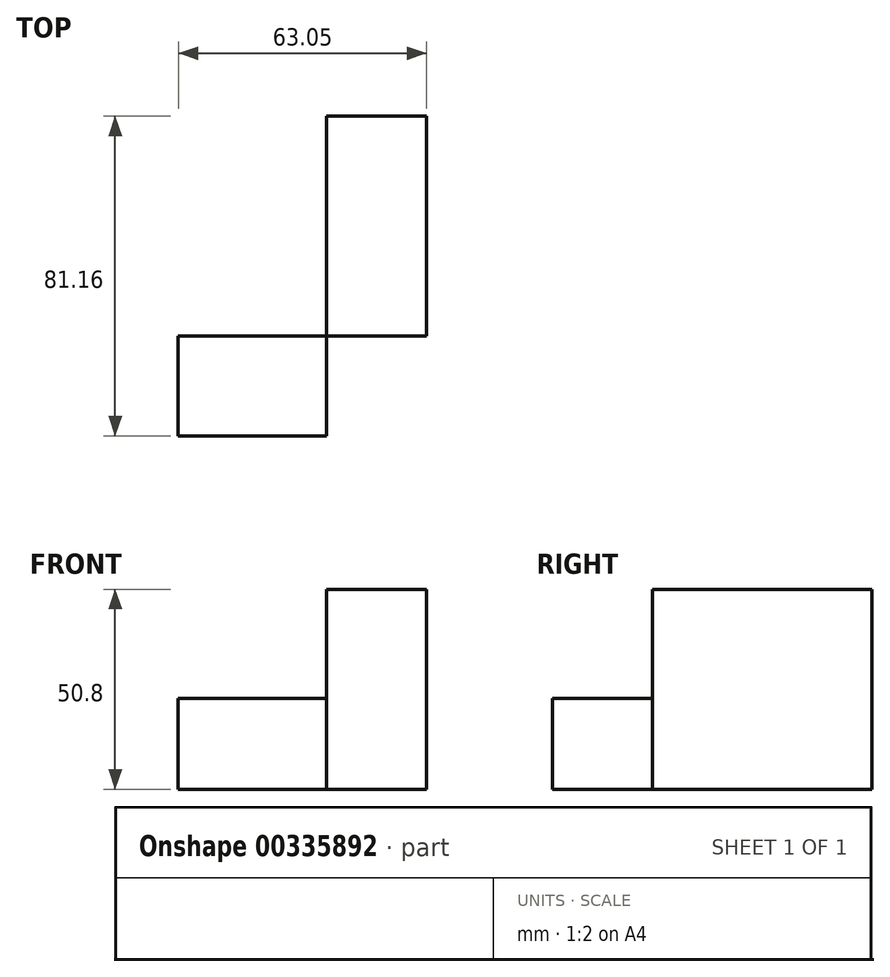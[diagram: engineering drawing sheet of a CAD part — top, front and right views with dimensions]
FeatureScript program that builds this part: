
annotation { "Feature Type Name" : "Feature", "Feature Type Description" : "" }
export const myFeature = defineFeature(function(context is Context, id is Id, definition is map)
    precondition{}
    {
        {
            var Q0;
            Q0=qCreatedBy(makeId("Right.planeOp"),FACE);
            var sketch = newSketch(context, id + "F0", { "sketchPlane" : qUnion([Q0])});
            skLineSegment(sketch, "E0", {"start": v(0, 0) * mm, "end": v(55.76, 0) * mm});
            skLineSegment(sketch, "E1", {"start": v(55.76, 0) * mm, "end": v(55.76, 50.8) * mm});
            skLineSegment(sketch, "E2", {"start": v(55.76, 50.8) * mm, "end": v(0, 50.8) * mm});
            skLineSegment(sketch, "E3", {"start": v(0, 50.8) * mm, "end": v(0, 0) * mm});
            skSolve(sketch);
        }
        {
            var Q0;
            Q0=makeQuery(id+"F0.imprint","IMPRINT",FACE,{"disambiguationData":[TD([[makeQuery(id+"F0.imprint","IMPRINT",EDGE,{"derivedFrom":sQuery(id+"F0.wireOp",EDGE,"E0")}),1.0]])]});
            extrude(context, id + "F1", {"entities" : qUnion([Q0]), "depth" : 25.4 * mm});
        }
        {
            var Q0;
            Q0=makeQuery(id+"F1.opExtrude","SWEPT_FACE",FACE,{"disambiguationData":[OSD([sQuery(id+"F0.wireOp",EDGE,"E3")])]});
            var sketch = newSketch(context, id + "F2", { "sketchPlane" : qUnion([Q0])});
            skLineSegment(sketch, "E4", {"start": v(0, 0) * mm, "end": v(-37.65, 0) * mm});
            skLineSegment(sketch, "E5", {"start": v(-37.65, 0) * mm, "end": v(-37.65, 23.08) * mm});
            skLineSegment(sketch, "E6", {"start": v(-37.65, 23.08) * mm, "end": v(0, 23.08) * mm});
            skLineSegment(sketch, "E7", {"start": v(0, 23.08) * mm, "end": v(0, 0) * mm});
            skSolve(sketch);
        }
        {
            var Q0;
            Q0=makeQuery(id+"F2.imprint","IMPRINT",FACE,{"disambiguationData":[TD([[makeQuery(id+"F2.imprint","IMPRINT",EDGE,{"derivedFrom":sQuery(id+"F2.wireOp",EDGE,"E4")}),-1.0]])]});
            extrude(context, id + "F3", {"entities" : qUnion([Q0]), "depth" : 25.4 * mm});
        }
    });
